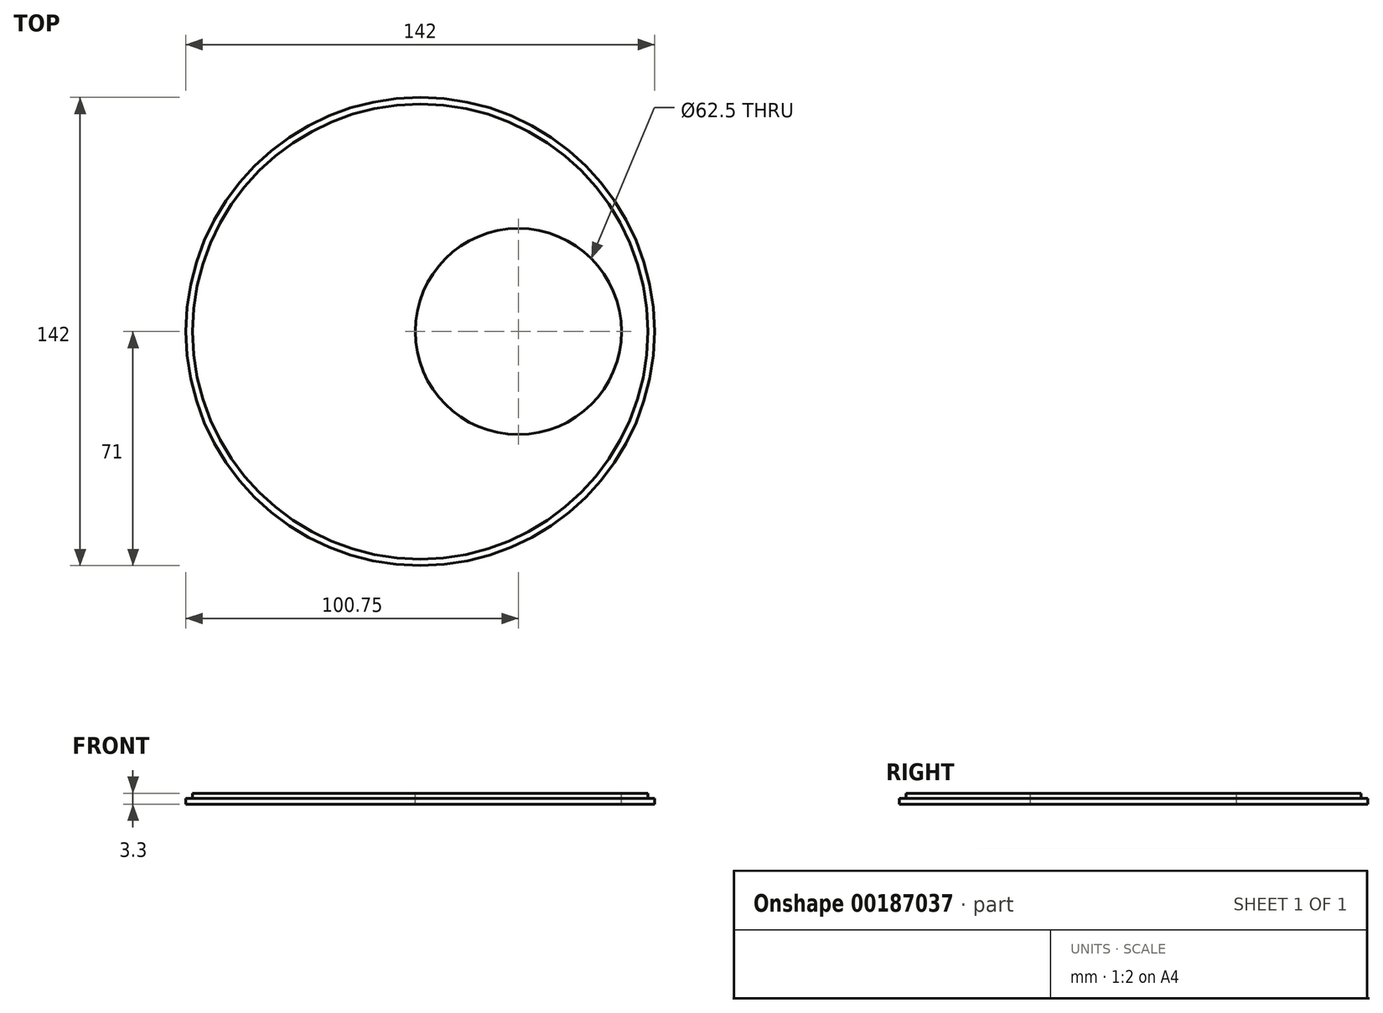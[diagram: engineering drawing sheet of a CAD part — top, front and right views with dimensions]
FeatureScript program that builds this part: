
annotation { "Feature Type Name" : "Feature", "Feature Type Description" : "" }
export const myFeature = defineFeature(function(context is Context, id is Id, definition is map)
    precondition{}
    {
        {
            var Q0;
            Q0=qCreatedBy(makeId("Top.planeOp"),FACE);
            var sketch = newSketch(context, id + "F0", { "sketchPlane" : qUnion([Q0])});
            skCircle(sketch, "E0", {"center": v(0, 0) * mm, "radius": 71 * mm});
            skSolve(sketch);
        }
        {
            var Q0;
            Q0 = qSketchRegion(id + "F0", true);
            extrude(context, id + "F1", {"entities" : qUnion([Q0]), "depth" : 1.7 * mm});
        }
        {
            var Q0;
            Q0=makeQuery(id+"F1.opExtrude","CAP_FACE",FACE,{"disambiguationData":[OSD([sQuery(id+"F0.wireOp",EDGE,"E0")])],"isStart":false});
            var sketch = newSketch(context, id + "F2", { "sketchPlane" : qUnion([Q0])});
            skCircle(sketch, "E1", {"center": v(0, 0) * mm, "radius": 69 * mm});
            skSolve(sketch);
        }
        {
            var Q0;
            Q0=makeQuery(id+"F2.imprint","IMPRINT",FACE,{"disambiguationData":[TD([[makeQuery(id+"F2.imprint","IMPRINT",EDGE,{"derivedFrom":sQuery(id+"F2.wireOp",EDGE,"E1")}),1.0]])]});
            extrude(context, id + "F3", {"entities" : qUnion([Q0]), "operationType" : NewBodyOperationType.ADD, "depth" : 1.6 * mm});
        }
        {
            var Q0;
            Q0=makeQuery(id+"F3.opExtrude","CAP_FACE",FACE,{"disambiguationData":[OSD([sQuery(id+"F2.wireOp",EDGE,"E1")])],"isStart":false});
            var sketch = newSketch(context, id + "F4", { "sketchPlane" : qUnion([Q0])});
            skCircle(sketch, "E2.0", {"center": v(0, 0) * mm, "radius": 61 * mm});
            skCircle(sketch, "E3", {"center": v(29.75, 0) * mm, "radius": 31.25 * mm});
            skSolve(sketch);
        }
        {
            var Q0;
            Q0=makeQuery(id+"F4.imprint","IMPRINT",FACE,{"disambiguationData":[TD([[makeQuery(id+"F4.imprint","IMPRINT",EDGE,{"derivedFrom":sQuery(id+"F4.wireOp",EDGE,"E3")}),1.0]])]});
            extrude(context, id + "F5", {"entities" : qUnion([Q0]), "operationType" : NewBodyOperationType.REMOVE, "oppositeDirection" : true, "depth" : 25 * mm});
        }
    });
